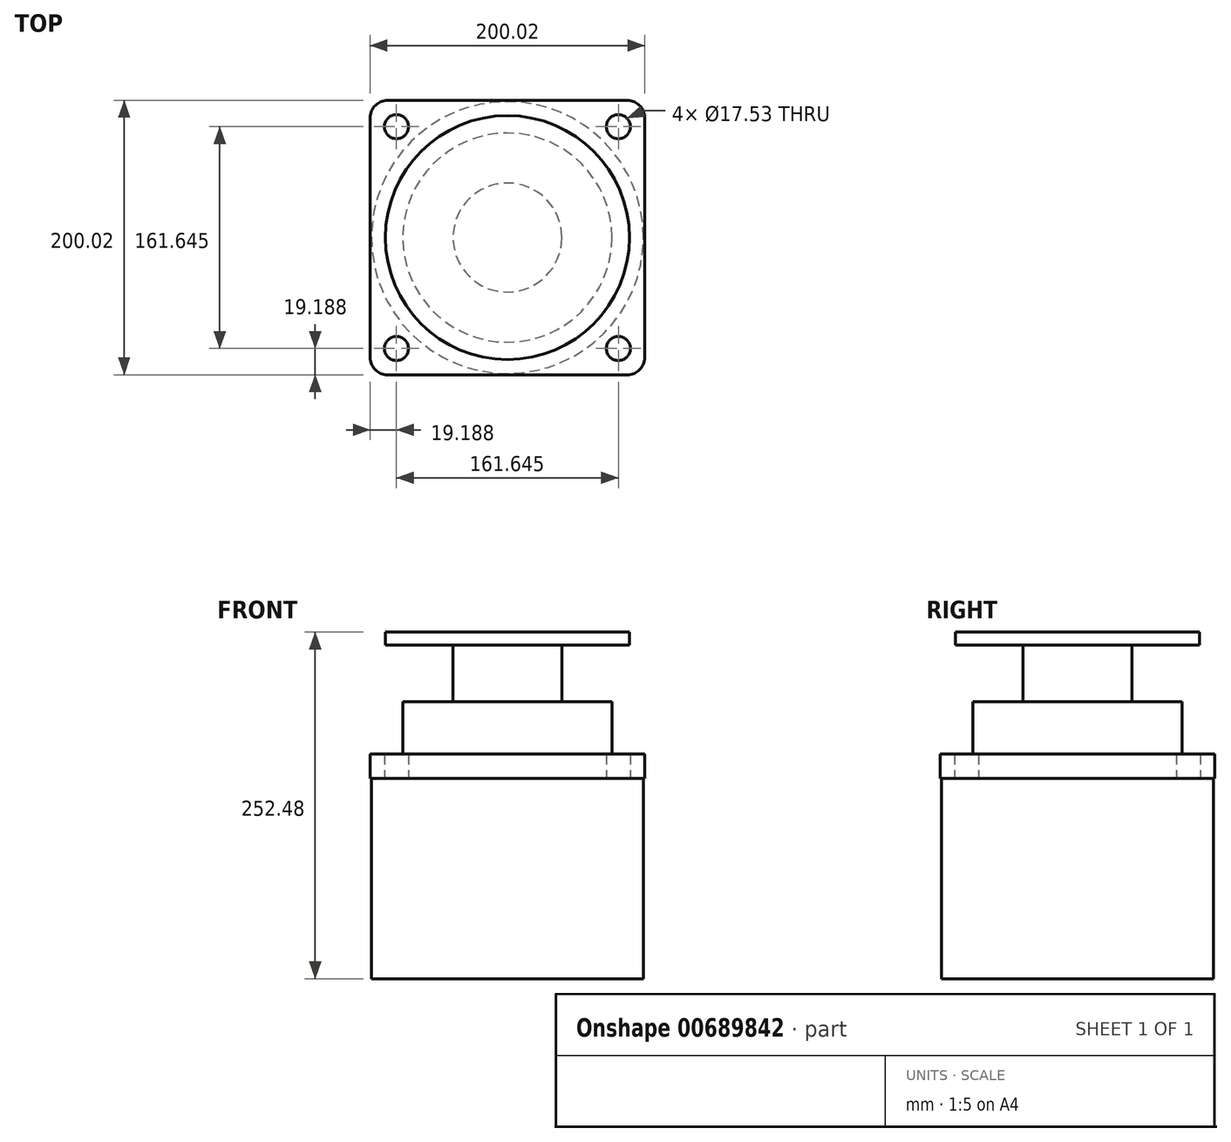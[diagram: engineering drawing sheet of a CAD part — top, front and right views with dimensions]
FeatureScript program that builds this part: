
annotation { "Feature Type Name" : "Feature", "Feature Type Description" : "" }
export const myFeature = defineFeature(function(context is Context, id is Id, definition is map)
    precondition{}
    {
        {
            var Q0;
            Q0=qCreatedBy(makeId("Top.planeOp"),FACE);
            var sketch = newSketch(context, id + "F0", { "sketchPlane" : qUnion([Q0])});
            skLineSegment(sketch, "E0.bottom", {"start": v(-87.31, 100.01) * mm, "end": v(87.31, 100.01) * mm});
            skLineSegment(sketch, "E0.top", {"start": v(-87.31, -100.01) * mm, "end": v(87.31, -100.01) * mm});
            skLineSegment(sketch, "E0.left", {"start": v(-100.01, 87.31) * mm, "end": v(-100.01, -87.31) * mm});
            skLineSegment(sketch, "E0.right", {"start": v(100.01, 87.31) * mm, "end": v(100.01, -87.31) * mm});
            skPoint(sketch, "E0.middle", {"position": v(0, 0) * mm});
            skPoint(sketch, "E1.visualSharp", {"position": v(-100.01, 100.01) * mm});
            skArc(sketch, "E1.filletArc", {"start": v(-87.31, 100.01) * mm, "mid": v(-96.3, 96.3) * mm, "end": v(-100.01, 87.31) * mm});
            skPoint(sketch, "E2.visualSharp", {"position": v(100.01, 100.01) * mm});
            skArc(sketch, "E2.filletArc", {"start": v(100.01, 87.31) * mm, "mid": v(96.3, 96.3) * mm, "end": v(87.31, 100.01) * mm});
            skPoint(sketch, "E3.visualSharp", {"position": v(100.01, -100.01) * mm});
            skArc(sketch, "E3.filletArc", {"start": v(87.31, -100.01) * mm, "mid": v(96.3, -96.3) * mm, "end": v(100.01, -87.31) * mm});
            skPoint(sketch, "E4.visualSharp", {"position": v(-100.01, -100.01) * mm});
            skArc(sketch, "E4.filletArc", {"start": v(-100.01, -87.31) * mm, "mid": v(-96.3, -96.3) * mm, "end": v(-87.31, -100.01) * mm});
            skCircle(sketch, "E5", {"center": v(0, 0) * mm, "radius": 114.3 * mm, "construction": true});
            skLineSegment(sketch, "E6", {"start": v(0, 0) * mm, "end": v(-80.82, 80.82) * mm, "construction": true});
            skLineSegment(sketch, "E7", {"start": v(0, 0) * mm, "end": v(0, 33.59) * mm, "construction": true});
            skCircle(sketch, "E8", {"center": v(-80.82, 80.82) * mm, "radius": 8.76 * mm});
            skCircle(sketch, "E9.1.0", {"center": v(-80.82, -80.82) * mm, "radius": 8.76 * mm});
            skCircle(sketch, "E9.2.0", {"center": v(80.82, -80.82) * mm, "radius": 8.76 * mm});
            skCircle(sketch, "E9.3.0", {"center": v(80.82, 80.82) * mm, "radius": 8.76 * mm});
            skSolve(sketch);
        }
        {
            var Q0;
            Q0 = qSketchRegion(id + "F0", true);
            extrude(context, id + "F1", {"entities" : qUnion([Q0]), "depth" : 17.53 * mm, "offsetDistance" : 25.4 * mm});
        }
        {
            var Q0;
            Q0=makeQuery(id+"F1.opExtrude","CAP_FACE",FACE,{"disambiguationData":[OSD([sQuery(id+"F0.wireOp",EDGE,"E0.bottom"),sQuery(id+"F0.wireOp",EDGE,"E0.top"),sQuery(id+"F0.wireOp",EDGE,"E0.left"),sQuery(id+"F0.wireOp",EDGE,"E0.right"),sQuery(id+"F0.wireOp",EDGE,"E1.filletArc"),sQuery(id+"F0.wireOp",EDGE,"E2.filletArc"),sQuery(id+"F0.wireOp",EDGE,"E3.filletArc"),sQuery(id+"F0.wireOp",EDGE,"E4.filletArc"),sQuery(id+"F0.wireOp",EDGE,"E8"),sQuery(id+"F0.wireOp",EDGE,"E9.1.0"),sQuery(id+"F0.wireOp",EDGE,"E9.2.0"),sQuery(id+"F0.wireOp",EDGE,"E9.3.0")])],"isStart":false});
            var sketch = newSketch(context, id + "F2", { "sketchPlane" : qUnion([Q0])});
            skCircle(sketch, "E10", {"center": v(0, 0) * mm, "radius": 99.06 * mm});
            skSolve(sketch);
        }
        {
            var Q0;
            Q0 = qSketchRegion(id + "F2", true);
            extrude(context, id + "F3", {"entities" : qUnion([Q0]), "operationType" : NewBodyOperationType.ADD, "oppositeDirection" : true, "depth" : 163.58 * mm, "offsetDistance" : 25.4 * mm});
        }
        {
            var Q0;
            Q0=makeQuery(id+"F1.opExtrude","CAP_FACE",FACE,{"disambiguationData":[OSD([sQuery(id+"F0.wireOp",EDGE,"E0.bottom"),sQuery(id+"F0.wireOp",EDGE,"E0.top"),sQuery(id+"F0.wireOp",EDGE,"E0.left"),sQuery(id+"F0.wireOp",EDGE,"E0.right"),sQuery(id+"F0.wireOp",EDGE,"E1.filletArc"),sQuery(id+"F0.wireOp",EDGE,"E2.filletArc"),sQuery(id+"F0.wireOp",EDGE,"E3.filletArc"),sQuery(id+"F0.wireOp",EDGE,"E4.filletArc"),sQuery(id+"F0.wireOp",EDGE,"E8"),sQuery(id+"F0.wireOp",EDGE,"E9.1.0"),sQuery(id+"F0.wireOp",EDGE,"E9.2.0"),sQuery(id+"F0.wireOp",EDGE,"E9.3.0")])],"isStart":false});
            var sketch = newSketch(context, id + "F4", { "sketchPlane" : qUnion([Q0])});
            skCircle(sketch, "E11", {"center": v(0, 0) * mm, "radius": 76.2 * mm});
            skSolve(sketch);
        }
        {
            var Q0;
            Q0 = qSketchRegion(id + "F4", true);
            extrude(context, id + "F5", {"entities" : qUnion([Q0]), "operationType" : NewBodyOperationType.ADD, "depth" : 38.1 * mm, "offsetDistance" : 25.4 * mm});
        }
        {
            var Q0;
            Q0=makeQuery(id+"F5.opExtrude","CAP_FACE",FACE,{"disambiguationData":[OSD([sQuery(id+"F4.wireOp",EDGE,"E11")])],"isStart":false});
            var sketch = newSketch(context, id + "F6", { "sketchPlane" : qUnion([Q0])});
            skCircle(sketch, "E12", {"center": v(0, 0) * mm, "radius": 39.69 * mm});
            skSolve(sketch);
        }
        {
            var Q0;
            Q0 = qSketchRegion(id + "F6", true);
            extrude(context, id + "F7", {"entities" : qUnion([Q0]), "operationType" : NewBodyOperationType.ADD, "depth" : 41.4 * mm, "offsetDistance" : 25.4 * mm});
        }
        {
            var Q0;
            Q0=makeQuery(id+"F1.opExtrude","CAP_FACE",FACE,{"disambiguationData":[OSD([sQuery(id+"F0.wireOp",EDGE,"E0.bottom"),sQuery(id+"F0.wireOp",EDGE,"E0.top"),sQuery(id+"F0.wireOp",EDGE,"E0.left"),sQuery(id+"F0.wireOp",EDGE,"E0.right"),sQuery(id+"F0.wireOp",EDGE,"E1.filletArc"),sQuery(id+"F0.wireOp",EDGE,"E2.filletArc"),sQuery(id+"F0.wireOp",EDGE,"E3.filletArc"),sQuery(id+"F0.wireOp",EDGE,"E4.filletArc"),sQuery(id+"F0.wireOp",EDGE,"E8"),sQuery(id+"F0.wireOp",EDGE,"E9.1.0"),sQuery(id+"F0.wireOp",EDGE,"E9.2.0"),sQuery(id+"F0.wireOp",EDGE,"E9.3.0")])],"isStart":false});
            cPlane(context, id + "F8", {"entities" : qUnion([Q0]), "cplaneType" : CPlaneType.OFFSET, "offset" : 88.9 * mm, "width" : 152.4 * mm, "height" : 152.4 * mm});
        }
        {
            var Q0;
            Q0=qCreatedBy(id+"F8.planeOp",FACE);
            var sketch = newSketch(context, id + "F9", { "sketchPlane" : qUnion([Q0])});
            skCircle(sketch, "E13", {"center": v(0, 0) * mm, "radius": 88.9 * mm});
            skSolve(sketch);
        }
        {
            var Q0;
            Q0=makeQuery(id+"F9.imprint","IMPRINT",FACE,{"disambiguationData":[TD([[makeQuery(id+"F9.imprint","IMPRINT",EDGE,{"derivedFrom":sQuery(id+"F9.wireOp",EDGE,"E13")}),1.0]])]});
            var Q1;
            Q1=sQuery(id+"F9.wireOp",EDGE,"E13");
            var Q2;
            Q2=makeQuery(id+"F7.opExtrude","CAP_FACE",FACE,{"disambiguationData":[OSD([sQuery(id+"F6.wireOp",EDGE,"E12")])],"isStart":false});
            extrude(context, id + "F10", {"entities" : qUnion([Q0]), "operationType" : NewBodyOperationType.ADD, "surfaceEntities" : qUnion([Q1]), "endBound" : BoundingType.UP_TO_SURFACE, "oppositeDirection" : true, "depth" : 25.4 * mm, "endBoundEntityFace" : qUnion([Q2]), "offsetDistance" : 25.4 * mm});
        }
    });
